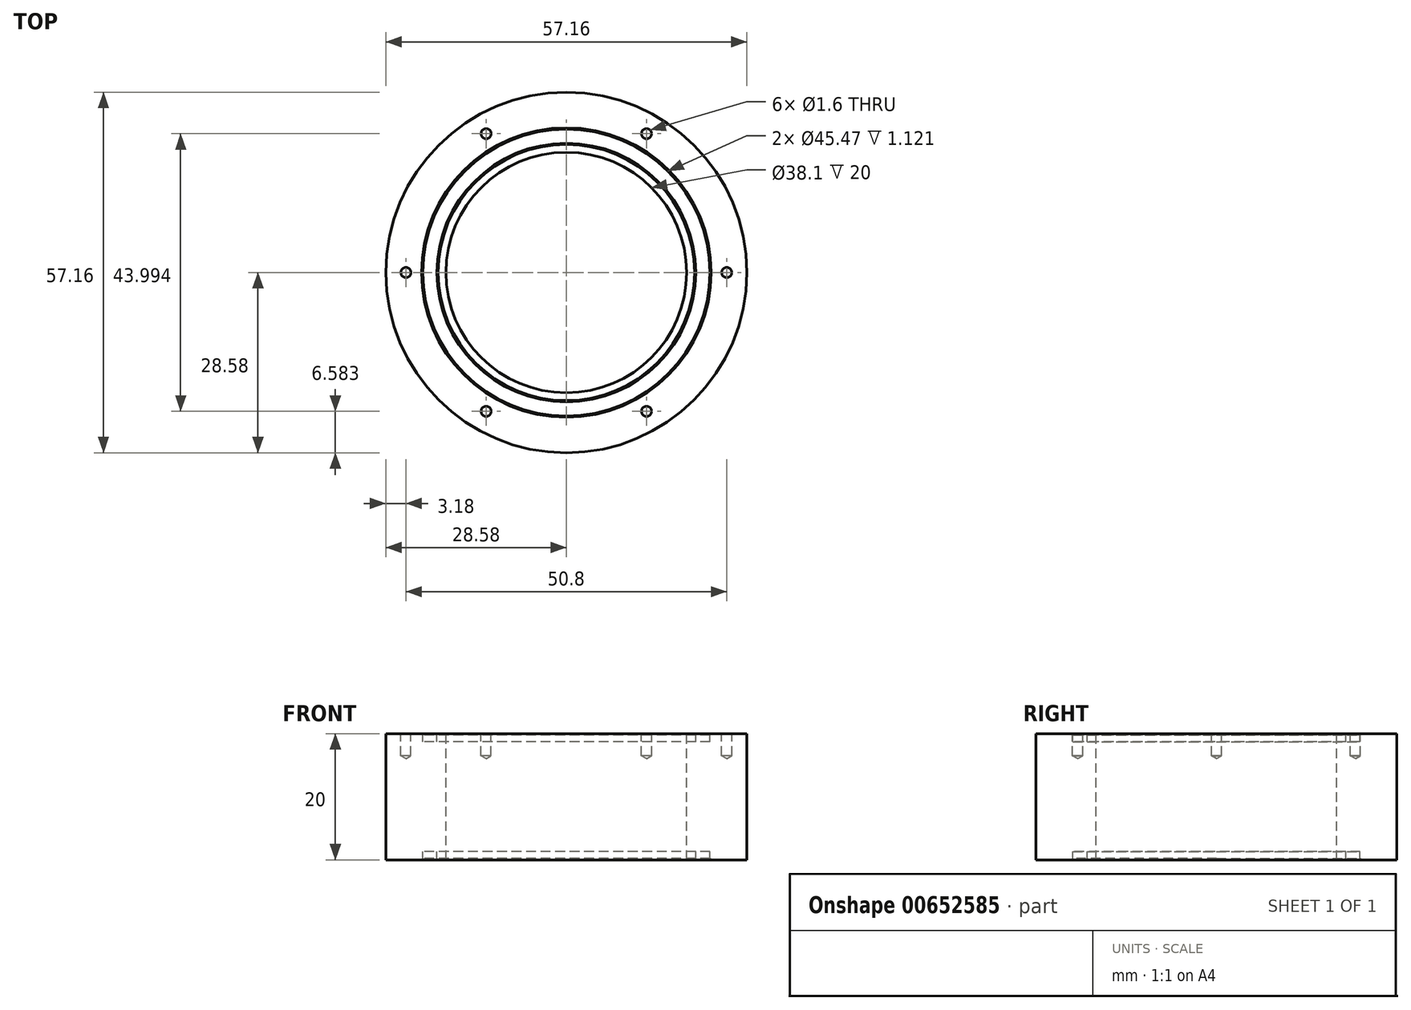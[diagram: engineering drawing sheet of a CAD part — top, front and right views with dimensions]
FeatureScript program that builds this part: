
annotation { "Feature Type Name" : "Feature", "Feature Type Description" : "" }
export const myFeature = defineFeature(function(context is Context, id is Id, definition is map)
    precondition{}
    {
        {
            var Q0;
            Q0=qCreatedBy(makeId("Right.planeOp"),FACE);
            var sketch = newSketch(context, id + "F0", { "sketchPlane" : qUnion([Q0])});
            skLineSegment(sketch, "E0", {"start": v(-28.58, 10) * mm, "end": v(-28.58, -10) * mm});
            skLineSegment(sketch, "E1", {"start": v(-28.58, -10) * mm, "end": v(-22.73, -10) * mm});
            skLineSegment(sketch, "E2", {"start": v(-22.73, -10) * mm, "end": v(-22.73, -8.68) * mm});
            skLineSegment(sketch, "E3", {"start": v(-22.73, -8.68) * mm, "end": v(-20.5, -8.68) * mm});
            skLineSegment(sketch, "E4", {"start": v(-20.5, -8.68) * mm, "end": v(-20.5, -10) * mm});
            skLineSegment(sketch, "E5", {"start": v(-20.5, -10) * mm, "end": v(-19.05, -10) * mm});
            skLineSegment(sketch, "E6", {"start": v(-19.05, -10) * mm, "end": v(-19.05, 10) * mm});
            skLineSegment(sketch, "E7", {"start": v(-19.05, 10) * mm, "end": v(-20.5, 10) * mm});
            skLineSegment(sketch, "E8", {"start": v(-20.5, 10) * mm, "end": v(-20.5, 8.68) * mm});
            skLineSegment(sketch, "E9", {"start": v(-20.5, 8.68) * mm, "end": v(-22.73, 8.68) * mm});
            skLineSegment(sketch, "E10", {"start": v(-22.73, 8.68) * mm, "end": v(-22.73, 10) * mm});
            skLineSegment(sketch, "E11", {"start": v(-22.73, 10) * mm, "end": v(-28.58, 10) * mm});
            skLineSegment(sketch, "E12", {"start": v(0, 10) * mm, "end": v(0, -10) * mm, "construction": true});
            skSolve(sketch);
        }
        {
            var Q0;
            Q0 = qSketchRegion(id + "F0", true);
            var Q1;
            Q1=sQuery(id+"F0.wireOp",EDGE,"E12");
            revolve(context, id + "F1", {"entities" : qUnion([Q0]), "axis" : qUnion([Q1]), "revolveType" : RevolveType.FULL});
        }
        {
            var Q0;
            Q0=makeQuery(id+"F1.opRevolve","SWEPT_EDGE",EDGE,{"disambiguationData":[OSD([sQuery(id+"F0.wireOp",EDGE,"E4"),sQuery(id+"F0.wireOp",EDGE,"E5")])]});
            var Q1;
            Q1=makeQuery(id+"F1.opRevolve","SWEPT_EDGE",EDGE,{"disambiguationData":[OSD([sQuery(id+"F0.wireOp",EDGE,"E1"),sQuery(id+"F0.wireOp",EDGE,"E2")])]});
            var Q2;
            Q2=makeQuery(id+"F1.opRevolve","SWEPT_EDGE",EDGE,{"disambiguationData":[OSD([sQuery(id+"F0.wireOp",EDGE,"E7"),sQuery(id+"F0.wireOp",EDGE,"E8")])]});
            var Q3;
            Q3=makeQuery(id+"F1.opRevolve","SWEPT_EDGE",EDGE,{"disambiguationData":[OSD([sQuery(id+"F0.wireOp",EDGE,"E10"),sQuery(id+"F0.wireOp",EDGE,"E11")])]});
            chamfer(context, id + "F2", {"entities" : qUnion([Q0, Q1, Q2, Q3]), "width" : .2 * mm, "tangentPropagation" : true});
        }
        {
            var Q0;
            Q0=makeQuery(id+"F1.opRevolve","SWEPT_FACE",FACE,{"disambiguationData":[OSD([sQuery(id+"F0.wireOp",EDGE,"E11")])]});
            var sketch = newSketch(context, id + "F3", { "sketchPlane" : qUnion([Q0])});
            skCircle(sketch, "E13", {"center": v(0, 0) * mm, "radius": 25.4 * mm, "construction": true});
            skPoint(sketch, "E14", {"position": v(-25.4, 0) * mm});
            skPoint(sketch, "E15.1.0", {"position": v(-12.7, -22) * mm});
            skPoint(sketch, "E15.2.0", {"position": v(12.7, -22) * mm});
            skPoint(sketch, "E15.3.0", {"position": v(25.4, 0) * mm});
            skPoint(sketch, "E15.4.0", {"position": v(12.7, 22) * mm});
            skPoint(sketch, "E15.5.0", {"position": v(-12.7, 22) * mm});
            skSolve(sketch);
        }
        {
            var Q0;
            Q0=sQuery(id+"F3.wireOp",VERTEX,"E15.5.0");
            var Q1;
            Q1=sQuery(id+"F3.wireOp",VERTEX,"E15.4.0");
            var Q2;
            Q2=sQuery(id+"F3.wireOp",VERTEX,"E15.3.0");
            var Q3;
            Q3=sQuery(id+"F3.wireOp",VERTEX,"E15.2.0");
            var Q4;
            Q4=sQuery(id+"F3.wireOp",VERTEX,"E15.1.0");
            var Q5;
            Q5=sQuery(id+"F3.wireOp",VERTEX,"E14");
            var Q6;
            Q6=makeQuery(id+"F1.opRevolve","SWEPT_BODY",BODY,{"disambiguationData":[OSD([sQuery(id+"F0.wireOp",EDGE,"E0"),sQuery(id+"F0.wireOp",EDGE,"E1"),sQuery(id+"F0.wireOp",EDGE,"E2"),sQuery(id+"F0.wireOp",EDGE,"E3"),sQuery(id+"F0.wireOp",EDGE,"E4"),sQuery(id+"F0.wireOp",EDGE,"E5"),sQuery(id+"F0.wireOp",EDGE,"E6"),sQuery(id+"F0.wireOp",EDGE,"E7"),sQuery(id+"F0.wireOp",EDGE,"E8"),sQuery(id+"F0.wireOp",EDGE,"E9"),sQuery(id+"F0.wireOp",EDGE,"E10"),sQuery(id+"F0.wireOp",EDGE,"E11")])]});
            hole(context, id + "F4", {"style" : HoleStyle.SIMPLE, "endStyle" : HoleEndStyle.BLIND, "holeDiameter" : 1.6 * mm, "majorDiameter" : 5 * mm, "holeDepth" : 3.5 * mm, "isTappedThrough" : true, "tappedDepth" : 12 * mm, "tapClearance" : 3, "locations" : qUnion([Q0, Q1, Q2, Q3, Q4, Q5]), "scope" : qUnion([Q6])});
        }
    });
